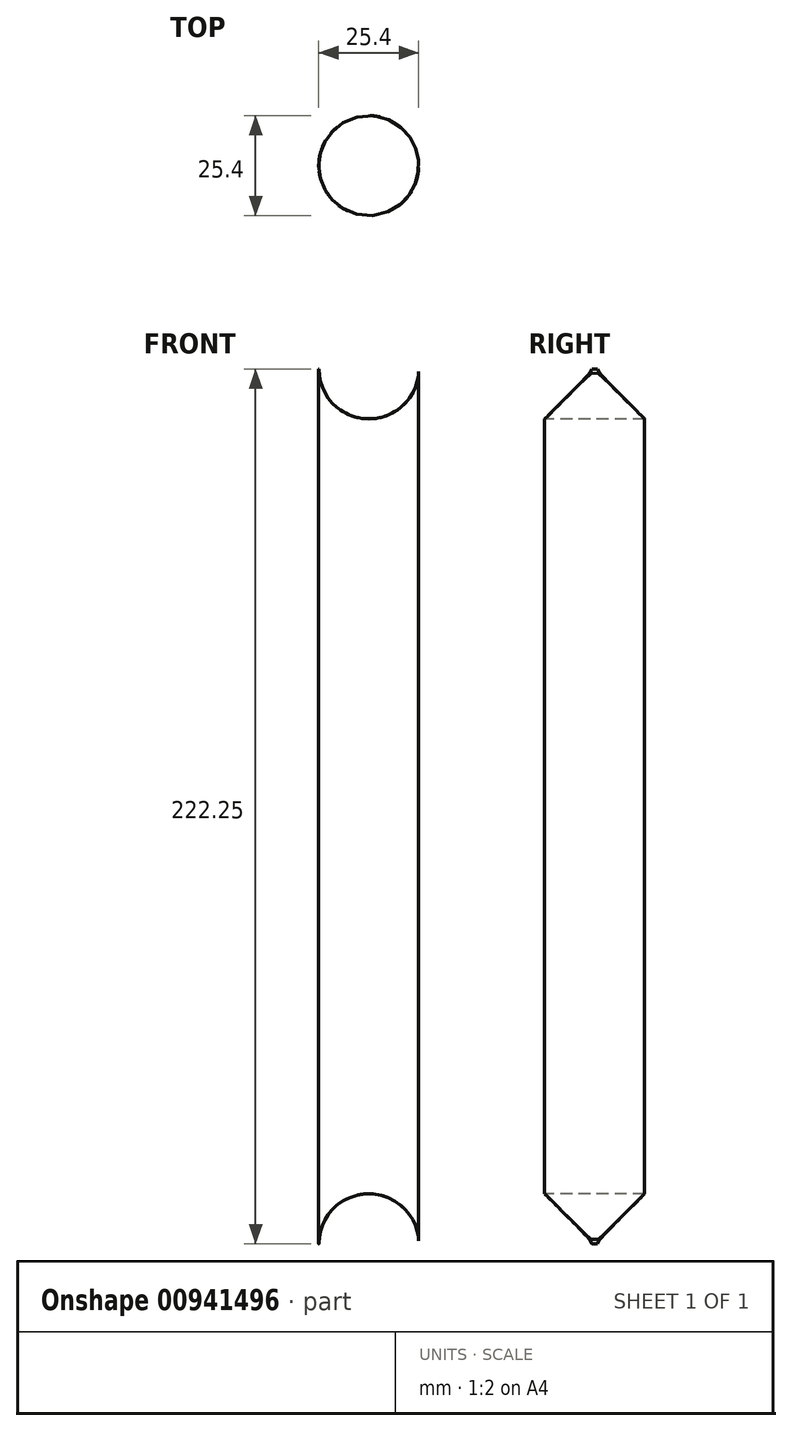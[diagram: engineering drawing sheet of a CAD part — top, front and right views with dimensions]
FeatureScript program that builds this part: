
annotation { "Feature Type Name" : "Feature", "Feature Type Description" : "" }
export const myFeature = defineFeature(function(context is Context, id is Id, definition is map)
    precondition{}
    {
        {
            var Q0;
            Q0=qCreatedBy(makeId("Front.planeOp"),FACE);
            var sketch = newSketch(context, id + "F0", { "sketchPlane" : qUnion([Q0])});
            skLineSegment(sketch, "E0.bottom", {"start": v(-6.48, 212.06) * mm, "end": v(6.22, 212.06) * mm});
            skLineSegment(sketch, "E0.top", {"start": v(-6.48, -10.19) * mm, "end": v(6.22, -10.19) * mm});
            skLineSegment(sketch, "E0.left", {"start": v(-6.48, 212.06) * mm, "end": v(-6.48, -10.19) * mm});
            skLineSegment(sketch, "E0.right", {"start": v(6.22, 212.06) * mm, "end": v(6.22, -10.19) * mm});
            skSolve(sketch);
        }
        {
            var Q0;
            Q0=qCreatedBy(makeId("Front.planeOp"),FACE);
            var sketch = newSketch(context, id + "F1", { "sketchPlane" : qUnion([Q0])});
            skCircle(sketch, "E1", {"center": v(6.23, 212.11) * mm, "radius": 12.7 * mm});
            skCircle(sketch, "E2", {"center": v(6.23, -10.16) * mm, "radius": 12.7 * mm});
            skSolve(sketch);
        }
        {
            var Q0;
            Q0=makeQuery(id+"F0.imprint","IMPRINT",FACE,{"disambiguationData":[TD([[makeQuery(id+"F0.imprint","IMPRINT",EDGE,{"derivedFrom":sQuery(id+"F0.wireOp",EDGE,"E0.bottom")}),-1.0]])]});
            var Q1;
            Q1=sQuery(id+"F0.wireOp",EDGE,"E0.right");
            revolve(context, id + "F2", {"surfaceOperationType" : NewSurfaceOperationType.NEW, "entities" : qUnion([Q0]), "axis" : qUnion([Q1]), "revolveType" : RevolveType.FULL});
        }
        {
            var Q0;
            Q0=makeQuery(id+"F1.imprint","IMPRINT",FACE,{"disambiguationData":[TD([[makeQuery(id+"F1.imprint","IMPRINT",EDGE,{"derivedFrom":sQuery(id+"F1.wireOp",EDGE,"E1")}),1.0]])]});
            var Q1;
            Q1=makeQuery(id+"F1.imprint","IMPRINT",FACE,{"disambiguationData":[TD([[makeQuery(id+"F1.imprint","IMPRINT",EDGE,{"derivedFrom":sQuery(id+"F1.wireOp",EDGE,"E2")}),1.0]])]});
            extrude(context, id + "F3", {"entities" : qUnion([Q0, Q1]), "operationType" : NewBodyOperationType.REMOVE, "endBound" : BoundingType.SYMMETRIC, "oppositeDirection" : true, "depth" : 25.4 * mm, "offsetDistance" : 25.4 * mm});
        }
    });
